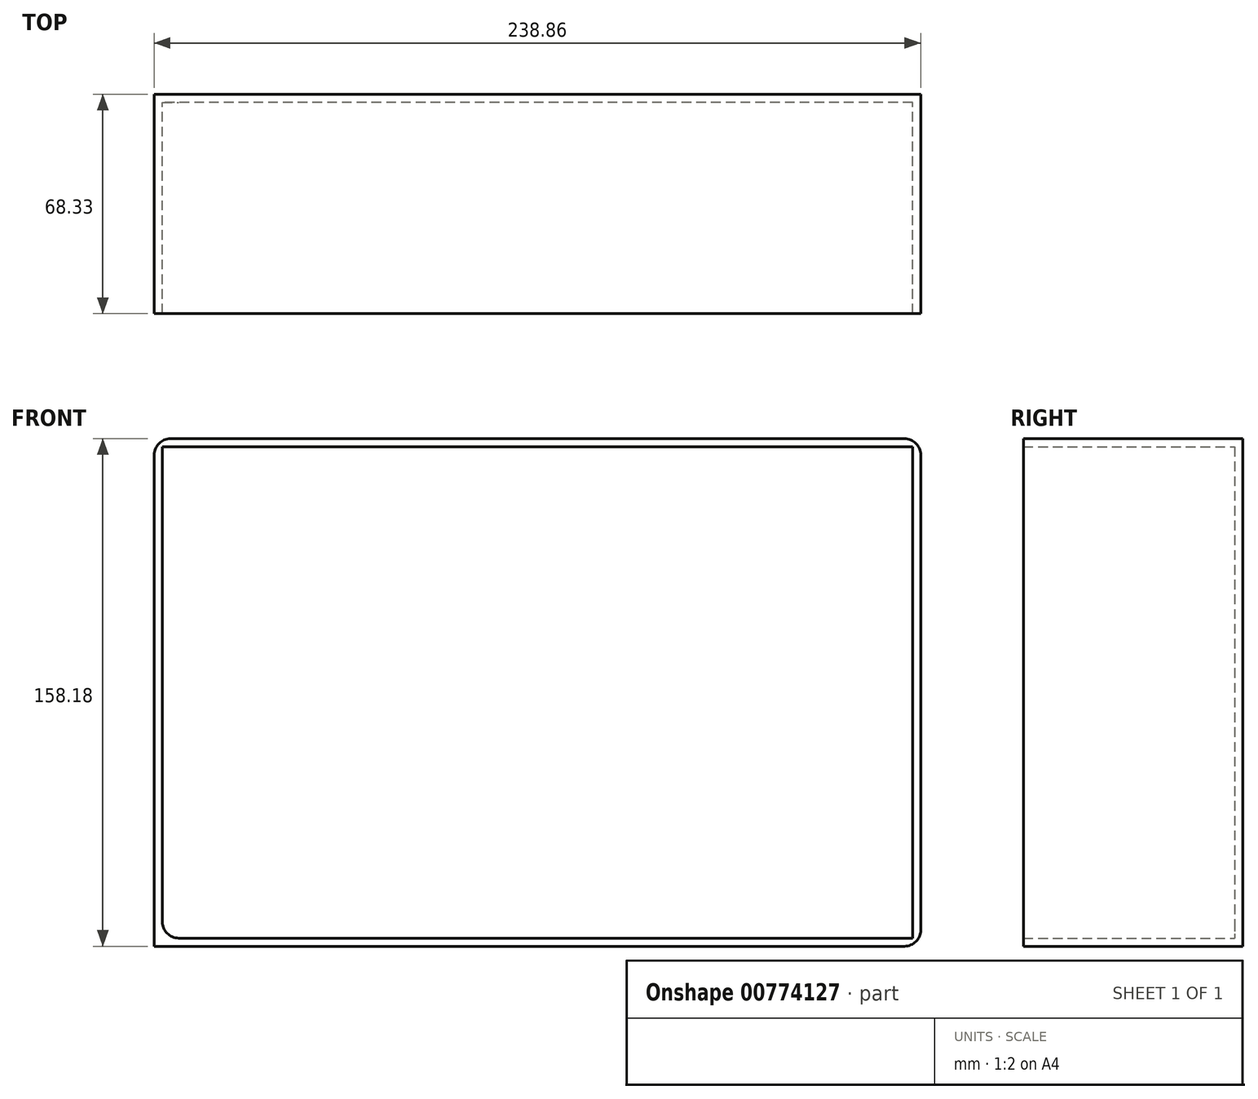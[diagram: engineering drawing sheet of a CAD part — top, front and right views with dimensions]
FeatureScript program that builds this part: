
annotation { "Feature Type Name" : "Feature", "Feature Type Description" : "" }
export const myFeature = defineFeature(function(context is Context, id is Id, definition is map)
    precondition{}
    {
        {
            var Q0;
            Q0=qCreatedBy(makeId("Front.planeOp"),FACE);
            var sketch = newSketch(context, id + "F0", { "sketchPlane" : qUnion([Q0])});
            skLineSegment(sketch, "E0.bottom", {"start": v(119.43, 79.09) * mm, "end": v(-119.43, 79.09) * mm});
            skLineSegment(sketch, "E0.top", {"start": v(119.43, -79.09) * mm, "end": v(-119.43, -79.09) * mm});
            skLineSegment(sketch, "E0.left", {"start": v(119.43, 79.09) * mm, "end": v(119.43, -79.09) * mm});
            skLineSegment(sketch, "E0.right", {"start": v(-119.43, 79.09) * mm, "end": v(-119.43, -79.09) * mm});
            skPoint(sketch, "E0.middle", {"position": v(0, 0) * mm});
            skSolve(sketch);
        }
        {
            var Q0;
            Q0=makeQuery(id+"F0.imprint","IMPRINT",FACE,{"disambiguationData":[TD([[makeQuery(id+"F0.imprint","IMPRINT",EDGE,{"derivedFrom":sQuery(id+"F0.wireOp",EDGE,"E0.bottom")}),1.0]])]});
            extrude(context, id + "F1", {"entities" : qUnion([Q0]), "depth" : 68.33 * mm, "offsetDistance" : 25.4 * mm});
        }
        {
            var Q0;
            Q0=makeQuery(id+"F1.opExtrude","CAP_FACE",FACE,{"disambiguationData":[OSD([sQuery(id+"F0.wireOp",EDGE,"E0.bottom"),sQuery(id+"F0.wireOp",EDGE,"E0.top"),sQuery(id+"F0.wireOp",EDGE,"E0.left"),sQuery(id+"F0.wireOp",EDGE,"E0.right")])],"isStart":false});
            shell(context, id + "F2", {"entities" : qUnion([Q0]), "thickness" : 2.54 * mm});
        }
        {
            var Q0;
            Q0=makeQuery(id+"F1.opExtrude","SWEPT_EDGE",EDGE,{"disambiguationData":[OSD([sQuery(id+"F0.wireOp",EDGE,"E0.bottom"),sQuery(id+"F0.wireOp",EDGE,"E0.right")])]});
            var Q1;
            Q1=makeQuery(id+"F1.opExtrude","SWEPT_EDGE",EDGE,{"disambiguationData":[OSD([sQuery(id+"F0.wireOp",EDGE,"E0.bottom"),sQuery(id+"F0.wireOp",EDGE,"E0.left")])]});
            var Q2;
            Q2=makeQuery(id+"F1.opExtrude","SWEPT_EDGE",EDGE,{"disambiguationData":[OSD([sQuery(id+"F0.wireOp",EDGE,"E0.top"),sQuery(id+"F0.wireOp",EDGE,"E0.left")])]});
            var Q3;
            Q3=makeQuery(id+"F2.opShell","OFFSET_EDGE",EDGE,{"disambiguationData":[OSD([sQuery(id+"F0.wireOp",EDGE,"E0.top"),sQuery(id+"F0.wireOp",EDGE,"E0.right")])]});
            fillet(context, id + "F3", {"entities" : qUnion([Q0, Q1, Q2, Q3]), "radius" : 5.08 * mm, "tangentPropagation" : true, "allowEdgeOverflow" : false});
        }
    });
